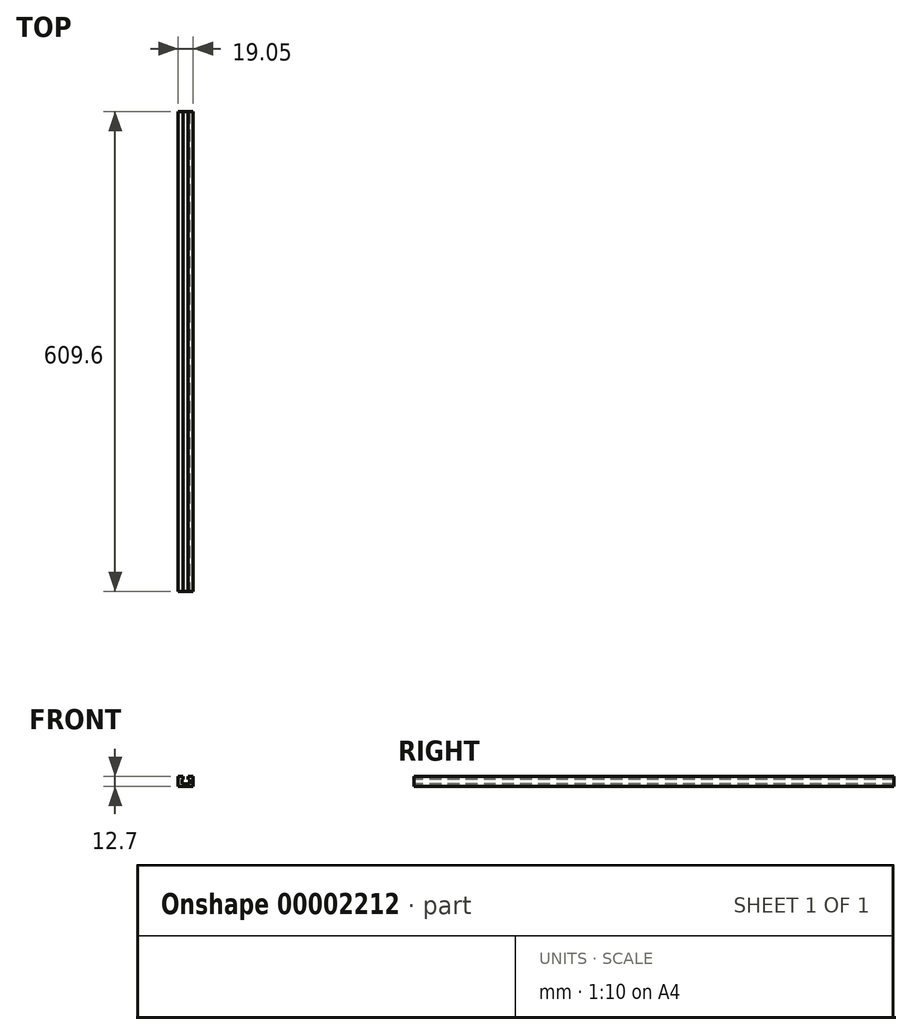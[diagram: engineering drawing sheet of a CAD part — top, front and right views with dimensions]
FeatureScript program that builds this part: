
annotation { "Feature Type Name" : "Feature", "Feature Type Description" : "" }
export const myFeature = defineFeature(function(context is Context, id is Id, definition is map)
    precondition{}
    {
        {
            var Q0;
            Q0=qCreatedBy(makeId("Front.planeOp"),FACE);
            var sketch = newSketch(context, id + "F0", { "sketchPlane" : qUnion([Q0])});
            skLineSegment(sketch, "E0", {"start": v(0, 0) * mm, "end": v(19.05, 0) * mm});
            skLineSegment(sketch, "E1", {"start": v(19.05, 0) * mm, "end": v(19.05, 12.7) * mm});
            skLineSegment(sketch, "E2", {"start": v(19.05, 12.7) * mm, "end": v(12.7, 12.7) * mm});
            skLineSegment(sketch, "E3", {"start": v(12.7, 12.7) * mm, "end": v(12.7, 9.07) * mm});
            skLineSegment(sketch, "E4", {"start": v(12.7, 9.07) * mm, "end": v(14.35, 9.07) * mm});
            skLineSegment(sketch, "E5", {"start": v(14.35, 9.07) * mm, "end": v(14.35, 3.44) * mm});
            skLineSegment(sketch, "E6", {"start": v(14.35, 3.44) * mm, "end": v(4.7, 3.44) * mm});
            skLineSegment(sketch, "E7", {"start": v(4.7, 3.44) * mm, "end": v(4.7, 8.95) * mm});
            skLineSegment(sketch, "E8", {"start": v(4.7, 8.95) * mm, "end": v(6.35, 8.95) * mm});
            skLineSegment(sketch, "E9", {"start": v(6.35, 8.95) * mm, "end": v(6.35, 12.7) * mm});
            skLineSegment(sketch, "E10", {"start": v(6.35, 12.7) * mm, "end": v(0, 12.7) * mm});
            skLineSegment(sketch, "E11", {"start": v(0, 12.7) * mm, "end": v(0, 0) * mm});
            skLineSegment(sketch, "E12", {"start": v(9.53, 0) * mm, "end": v(9.53, 17.44) * mm, "construction": true});
            skSolve(sketch);
        }
        {
            var Q0;
            Q0=makeQuery(id+"F0.imprint","IMPRINT",FACE,{"disambiguationData":[TD([[makeQuery(id+"F0.imprint","IMPRINT",EDGE,{"derivedFrom":sQuery(id+"F0.wireOp",EDGE,"E0")}),1.0]])]});
            extrude(context, id + "F1", {"entities" : qUnion([Q0]), "oppositeDirection" : true, "depth" : 609.6 * mm});
        }
    });
